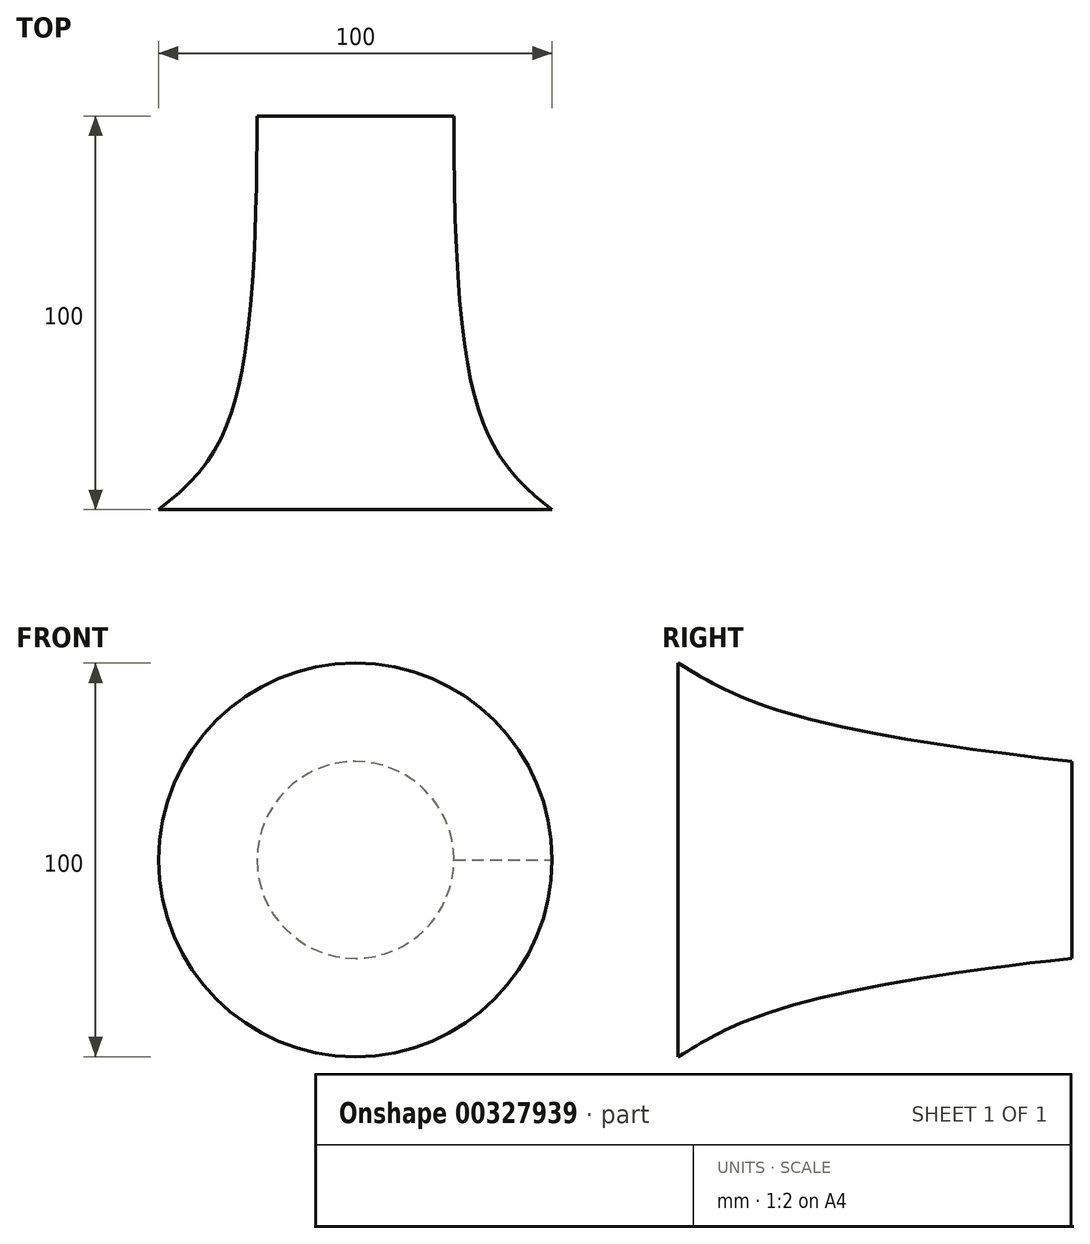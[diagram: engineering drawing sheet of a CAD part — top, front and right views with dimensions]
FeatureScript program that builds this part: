
annotation { "Feature Type Name" : "Feature", "Feature Type Description" : "" }
export const myFeature = defineFeature(function(context is Context, id is Id, definition is map)
    precondition{}
    {
        {
            var Q0;
            Q0=qCreatedBy(makeId("Front.planeOp"),FACE);
            var sketch = newSketch(context, id + "F0", { "sketchPlane" : qUnion([Q0])});
            skCircle(sketch, "E0", {"center": v(0, 0) * mm, "radius": 25 * mm});
            skSolve(sketch);
        }
        {
            var Q0;
            Q0=qCreatedBy(makeId("Front.planeOp"),FACE);
            cPlane(context, id + "F1", {"entities" : qUnion([Q0]), "cplaneType" : CPlaneType.OFFSET, "offset" : 100 * mm, "width" : 150 * mm, "height" : 150 * mm});
        }
        {
            var Q0;
            Q0=qCreatedBy(id+"F1.planeOp",FACE);
            var sketch = newSketch(context, id + "F2", { "sketchPlane" : qUnion([Q0])});
            skPoint(sketch, "E1.0", {"position": v(0, 0) * mm});
            skCircle(sketch, "E1.1", {"center": v(0, 0) * mm, "radius": 25 * mm, "construction": true});
            skCircle(sketch, "E2", {"center": v(0, 0) * mm, "radius": 50 * mm});
            skSolve(sketch);
        }
        {
            var Q0;
            Q0=qCreatedBy(makeId("Top.planeOp"),FACE);
            var sketch = newSketch(context, id + "F3", { "sketchPlane" : qUnion([Q0])});
            skLineSegment(sketch, "E3.0", {"start": v(50, -100) * mm, "end": v(-50, -100) * mm, "construction": true});
            skLineSegment(sketch, "E3.1", {"start": v(25, 0) * mm, "end": v(-25, 0) * mm, "construction": true});
            skFitSpline(sketch, "E4", {"points": [v(-25, 0) * mm, v(-50, -100) * mm], "startDerivative": vector(0, -225) * mm, "endDerivative": vector(-54, -42) * mm});
            skLineSegment(sketch, "E5", {"start": v(0, 0) * mm, "end": v(0, -100) * mm, "construction": true});
            skFitSpline(sketch, "E6.MirrorCS", {"points": [v(25, 0) * mm, v(50, -100) * mm], "startDerivative": vector(0, -225) * mm, "endDerivative": vector(54, -42) * mm});
            skSolve(sketch);
        }
        {
            var Q0;
            Q0=makeQuery(id+"F0.imprint","IMPRINT",FACE,{"disambiguationData":[TD([[makeQuery(id+"F0.imprint","IMPRINT",EDGE,{"derivedFrom":sQuery(id+"F0.wireOp",EDGE,"E0")}),1.0]])]});
            var Q1;
            Q1=makeQuery(id+"F2.imprint","IMPRINT",FACE,{"disambiguationData":[TD([[makeQuery(id+"F2.imprint","IMPRINT",EDGE,{"derivedFrom":sQuery(id+"F2.wireOp",EDGE,"E2")}),1.0]])]});
            var Q2;
            Q2=sQuery(id+"F3.wireOp",EDGE,"E6.MirrorCS");
            var Q3;
            Q3=sQuery(id+"F3.wireOp",EDGE,"E4");
            loft(context, id + "F4", {"addGuides" : true, "sheetProfilesArray" : [{ "sheetProfileEntities" : qUnion([Q0]) }, { "sheetProfileEntities" : qUnion([Q1]) }], "guidesArray" : [{ "guideEntities" : qUnion([Q2]), "guideDerivativeType" : LoftGuideDerivativeType.DEFAULT, "guideDerivativeMagnitude" : 1 }, { "guideEntities" : qUnion([Q3]), "guideDerivativeType" : LoftGuideDerivativeType.DEFAULT, "guideDerivativeMagnitude" : 1 }]});
        }
    });
